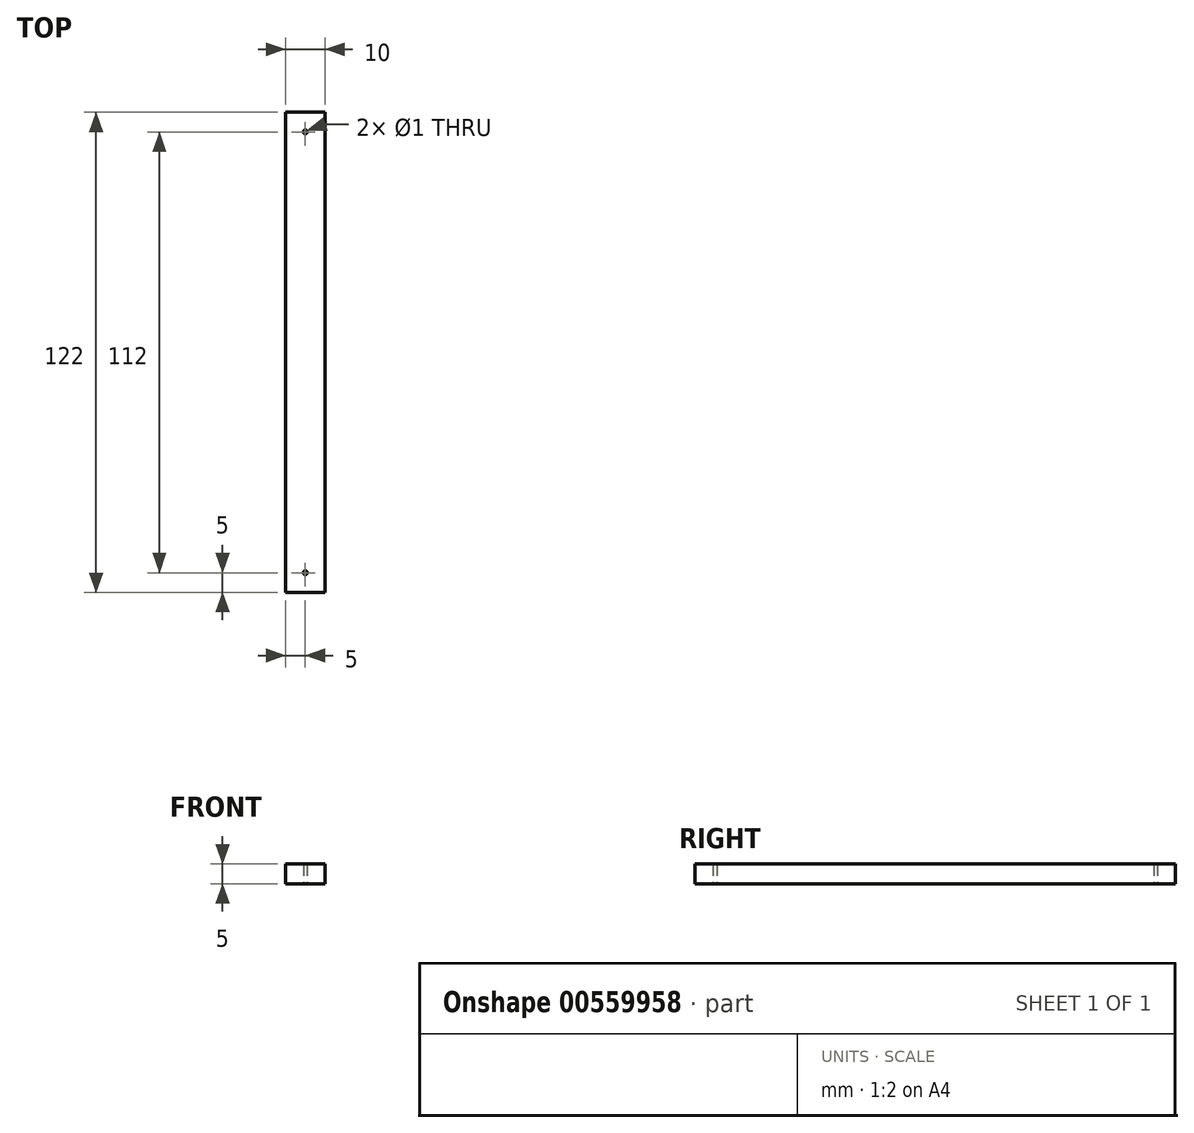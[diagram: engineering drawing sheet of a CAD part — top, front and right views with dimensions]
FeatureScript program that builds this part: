
annotation { "Feature Type Name" : "Feature", "Feature Type Description" : "" }
export const myFeature = defineFeature(function(context is Context, id is Id, definition is map)
    precondition{}
    {
        {
            var Q0;
            Q0=qCreatedBy(makeId("Top.planeOp"),FACE);
            var sketch = newSketch(context, id + "F0", { "sketchPlane" : qUnion([Q0])});
            skLineSegment(sketch, "E0.bottom", {"start": v(0, 0) * mm, "end": v(10, 0) * mm});
            skLineSegment(sketch, "E0.top", {"start": v(0, 122) * mm, "end": v(10, 122) * mm});
            skLineSegment(sketch, "E0.left", {"start": v(0, 0) * mm, "end": v(0, 122) * mm});
            skLineSegment(sketch, "E0.right", {"start": v(10, 0) * mm, "end": v(10, 122) * mm});
            skCircle(sketch, "E1", {"center": v(5, 117) * mm, "radius": 0.5 * mm});
            skCircle(sketch, "E2", {"center": v(5, 5) * mm, "radius": 0.5 * mm});
            skPoint(sketch, "E2.centerSnap0", {"position": v(5, 0) * mm});
            skSolve(sketch);
        }
        {
            var Q0;
            Q0 = qSketchRegion(id + "F0", true);
            extrude(context, id + "F1", {"entities" : qUnion([Q0]), "depth" : 5 * mm, "offsetDistance" : 25 * mm});
        }
    });
